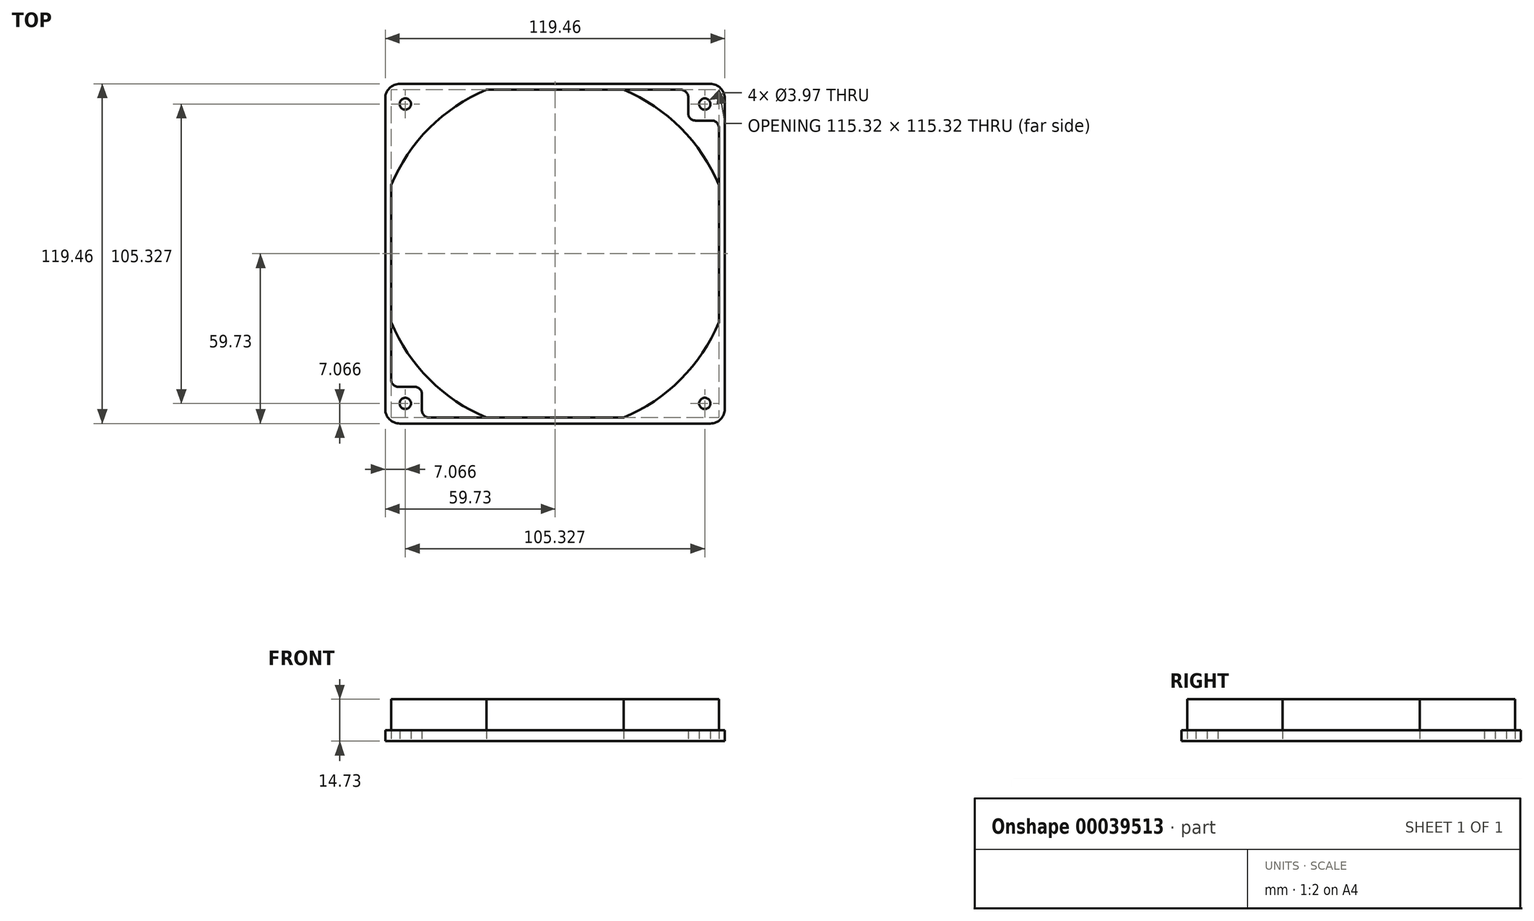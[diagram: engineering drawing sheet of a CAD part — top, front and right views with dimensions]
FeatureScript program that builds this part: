
annotation { "Feature Type Name" : "Feature", "Feature Type Description" : "" }
export const myFeature = defineFeature(function(context is Context, id is Id, definition is map)
    precondition{}
    {
        {
            var Q0;
            Q0=qCreatedBy(makeId("Top.planeOp"),FACE);
            var sketch = newSketch(context, id + "F0", { "sketchPlane" : qUnion([Q0])});
            skLineSegment(sketch, "E0", {"start": v(0, 0) * mm, "end": v(0, 233.62) * mm, "construction": true});
            skLineSegment(sketch, "E1.rect.bottom", {"start": v(-59.73, 59.73) * mm, "end": v(59.73, 59.73) * mm, "construction": true});
            skLineSegment(sketch, "E1.rect.top", {"start": v(-59.73, -59.73) * mm, "end": v(59.73, -59.73) * mm, "construction": true});
            skLineSegment(sketch, "E1.rect.left", {"start": v(-59.73, 59.73) * mm, "end": v(-59.73, -59.73) * mm, "construction": true});
            skLineSegment(sketch, "E1.rect.right", {"start": v(59.73, 59.73) * mm, "end": v(59.73, -59.73) * mm, "construction": true});
            skPoint(sketch, "E1.rect.middle", {"position": v(0, 0) * mm});
            skCircle(sketch, "E2", {"center": v(0, 0) * mm, "radius": 57.66 * mm, "construction": true});
            skLineSegment(sketch, "E3", {"start": v(-59.73, 0) * mm, "end": v(-59.73, 54.65) * mm});
            skLineSegment(sketch, "E4", {"start": v(0, 59.73) * mm, "end": v(-54.65, 59.73) * mm});
            skCircle(sketch, "E5", {"center": v(-52.66, 52.66) * mm, "radius": 1.98 * mm});
            skArc(sketch, "E6", {"start": v(-57.66, 0) * mm, "mid": v(-40.77, 40.77) * mm, "end": v(0, 57.66) * mm});
            skLineSegment(sketch, "E7", {"start": v(-57.66, 0) * mm, "end": v(-57.66, 44.3) * mm});
            skLineSegment(sketch, "E8", {"start": v(-55.12, 46.83) * mm, "end": v(-49.37, 46.83) * mm});
            skLineSegment(sketch, "E9", {"start": v(-46.83, 49.37) * mm, "end": v(-46.83, 55.12) * mm});
            skLineSegment(sketch, "E10", {"start": v(-44.3, 57.66) * mm, "end": v(0, 57.66) * mm});
            skArc(sketch, "E11", {"start": v(-57.66, 29.09) * mm, "mid": v(-45.66, 45.66) * mm, "end": v(-29.09, 57.66) * mm, "construction": true});
            skPoint(sketch, "E12.visualSharp", {"position": v(-57.66, 46.83) * mm});
            skArc(sketch, "E12.filletArc", {"start": v(-55.12, 46.83) * mm, "mid": v(-56.91, 46.09) * mm, "end": v(-57.66, 44.3) * mm});
            skPoint(sketch, "E13.visualSharp", {"position": v(-46.83, 46.83) * mm});
            skArc(sketch, "E13.filletArc", {"start": v(-49.37, 46.83) * mm, "mid": v(-47.58, 47.58) * mm, "end": v(-46.83, 49.37) * mm});
            skPoint(sketch, "E14.visualSharp", {"position": v(-46.83, 57.66) * mm});
            skArc(sketch, "E14.filletArc", {"start": v(-44.3, 57.66) * mm, "mid": v(-46.09, 56.91) * mm, "end": v(-46.83, 55.12) * mm});
            skPoint(sketch, "E15.visualSharp", {"position": v(-59.73, 59.73) * mm});
            skArc(sketch, "E15.filletArc", {"start": v(-54.65, 59.73) * mm, "mid": v(-58.24, 58.24) * mm, "end": v(-59.73, 54.65) * mm});
            skLineSegment(sketch, "E16", {"start": v(0, 0) * mm, "end": v(-142.77, 0) * mm, "construction": true});
            skArc(sketch, "E17.MirrorCS", {"start": v(49.37, 46.83) * mm, "mid": v(47.58, 47.58) * mm, "end": v(46.83, 49.37) * mm});
            skArc(sketch, "E18.MirrorCS", {"start": v(44.3, 57.66) * mm, "mid": v(46.09, 56.91) * mm, "end": v(46.83, 55.12) * mm});
            skLineSegment(sketch, "E19.MirrorCS", {"start": v(55.12, 46.83) * mm, "end": v(49.37, 46.83) * mm});
            skLineSegment(sketch, "E20.MirrorCS", {"start": v(46.83, 49.37) * mm, "end": v(46.83, 55.12) * mm});
            skCircle(sketch, "E21.MirrorC", {"center": v(52.66, 52.66) * mm, "radius": 1.98 * mm});
            skArc(sketch, "E22.MirrorCS", {"start": v(54.65, 59.73) * mm, "mid": v(58.24, 58.24) * mm, "end": v(59.73, 54.65) * mm});
            skArc(sketch, "E23.MirrorCS", {"start": v(55.12, 46.83) * mm, "mid": v(56.91, 46.09) * mm, "end": v(57.66, 44.3) * mm});
            skPoint(sketch, "E24.MirrorP", {"position": v(59.73, 59.73) * mm});
            skLineSegment(sketch, "E25.MirrorCS", {"start": v(57.66, 0) * mm, "end": v(57.66, 44.3) * mm});
            skArc(sketch, "E26.MirrorCS", {"start": v(57.66, 0) * mm, "mid": v(40.77, 40.77) * mm, "end": v(0, 57.66) * mm});
            skPoint(sketch, "E27.MirrorP", {"position": v(46.83, 57.66) * mm});
            skLineSegment(sketch, "E28.MirrorCS", {"start": v(59.73, 0) * mm, "end": v(59.73, 54.65) * mm});
            skLineSegment(sketch, "E29.MirrorCS", {"start": v(44.3, 57.66) * mm, "end": v(0, 57.66) * mm});
            skLineSegment(sketch, "E30.MirrorCS", {"start": v(0, 59.73) * mm, "end": v(54.65, 59.73) * mm});
            skArc(sketch, "E31.MirrorCS", {"start": v(57.66, 29.09) * mm, "mid": v(45.66, 45.66) * mm, "end": v(29.09, 57.66) * mm, "construction": true});
            skPoint(sketch, "E32.MirrorP", {"position": v(46.83, 46.83) * mm});
            skPoint(sketch, "E33.MirrorP", {"position": v(57.66, 46.83) * mm});
            skLineSegment(sketch, "E34.MirrorCS", {"start": v(-59.73, -59.73) * mm, "end": v(59.73, -59.73) * mm});
            skLineSegment(sketch, "E35.MirrorCS", {"start": v(55.12, -46.83) * mm, "end": v(49.37, -46.83) * mm});
            skArc(sketch, "E36.MirrorCS", {"start": v(54.65, -59.73) * mm, "mid": v(58.24, -58.24) * mm, "end": v(59.73, -54.65) * mm});
            skArc(sketch, "E37.MirrorCS", {"start": v(49.37, -46.83) * mm, "mid": v(47.58, -47.58) * mm, "end": v(46.83, -49.37) * mm});
            skArc(sketch, "E38.MirrorCS", {"start": v(-49.37, -46.83) * mm, "mid": v(-47.58, -47.58) * mm, "end": v(-46.83, -49.37) * mm});
            skArc(sketch, "E39.MirrorCS", {"start": v(-44.3, -57.66) * mm, "mid": v(-46.09, -56.91) * mm, "end": v(-46.83, -55.12) * mm});
            skLineSegment(sketch, "E40.MirrorCS", {"start": v(46.83, -49.37) * mm, "end": v(46.83, -55.12) * mm});
            skArc(sketch, "E41.MirrorCS", {"start": v(55.12, -46.83) * mm, "mid": v(56.91, -46.09) * mm, "end": v(57.66, -44.3) * mm});
            skArc(sketch, "E42.MirrorCS", {"start": v(-54.65, -59.73) * mm, "mid": v(-58.24, -58.24) * mm, "end": v(-59.73, -54.65) * mm});
            skArc(sketch, "E43.MirrorCS", {"start": v(44.3, -57.66) * mm, "mid": v(46.09, -56.91) * mm, "end": v(46.83, -55.12) * mm});
            skLineSegment(sketch, "E44.MirrorCS", {"start": v(-55.12, -46.83) * mm, "end": v(-49.37, -46.83) * mm});
            skLineSegment(sketch, "E45.MirrorCS", {"start": v(-46.83, -49.37) * mm, "end": v(-46.83, -55.12) * mm});
            skArc(sketch, "E46.MirrorCS", {"start": v(-55.12, -46.83) * mm, "mid": v(-56.91, -46.09) * mm, "end": v(-57.66, -44.3) * mm});
            skCircle(sketch, "E47.MirrorC", {"center": v(52.66, -52.66) * mm, "radius": 1.98 * mm});
            skCircle(sketch, "E48.MirrorC", {"center": v(-52.66, -52.66) * mm, "radius": 1.98 * mm});
            skArc(sketch, "E49.MirrorCS", {"start": v(57.66, 0) * mm, "mid": v(40.77, -40.77) * mm, "end": v(0, -57.66) * mm});
            skLineSegment(sketch, "E50.MirrorCS", {"start": v(57.66, 0) * mm, "end": v(57.66, -44.3) * mm});
            skArc(sketch, "E51.MirrorCS", {"start": v(-57.66, -29.09) * mm, "mid": v(-45.66, -45.66) * mm, "end": v(-29.09, -57.66) * mm, "construction": true});
            skArc(sketch, "E52.MirrorCS", {"start": v(57.66, -29.09) * mm, "mid": v(45.66, -45.66) * mm, "end": v(29.09, -57.66) * mm, "construction": true});
            skPoint(sketch, "E53.MirrorP", {"position": v(57.66, -46.83) * mm});
            skPoint(sketch, "E54.MirrorP", {"position": v(-57.66, -46.83) * mm});
            skPoint(sketch, "E55.MirrorP", {"position": v(59.73, -59.73) * mm});
            skLineSegment(sketch, "E56.MirrorCS", {"start": v(-59.73, 0) * mm, "end": v(-59.73, -54.65) * mm});
            skPoint(sketch, "E57.MirrorP", {"position": v(-59.73, -59.73) * mm});
            skLineSegment(sketch, "E58.MirrorCS", {"start": v(59.73, 0) * mm, "end": v(59.73, -54.65) * mm});
            skLineSegment(sketch, "E59.MirrorCS", {"start": v(-44.3, -57.66) * mm, "end": v(0, -57.66) * mm});
            skPoint(sketch, "E60.MirrorP", {"position": v(-46.83, -46.83) * mm});
            skLineSegment(sketch, "E61.MirrorCS", {"start": v(0, -59.73) * mm, "end": v(-54.65, -59.73) * mm});
            skLineSegment(sketch, "E62.MirrorCS", {"start": v(0, -59.73) * mm, "end": v(54.65, -59.73) * mm});
            skPoint(sketch, "E63.MirrorP", {"position": v(46.83, -57.66) * mm});
            skArc(sketch, "E64.MirrorCS", {"start": v(-57.66, 0) * mm, "mid": v(-40.77, -40.77) * mm, "end": v(0, -57.66) * mm});
            skLineSegment(sketch, "E65.MirrorCS", {"start": v(-57.66, 0) * mm, "end": v(-57.66, -44.3) * mm});
            skPoint(sketch, "E66.MirrorP", {"position": v(46.83, -46.83) * mm});
            skLineSegment(sketch, "E67.MirrorCS", {"start": v(44.3, -57.66) * mm, "end": v(0, -57.66) * mm});
            skPoint(sketch, "E68.MirrorP", {"position": v(-46.83, -57.66) * mm});
            skArc(sketch, "E69", {"start": v(-57.66, 24.14) * mm, "mid": v(-44.2, 44.2) * mm, "end": v(-24.14, 57.66) * mm});
            skLineSegment(sketch, "E70", {"start": v(-59.73, 0) * mm, "end": v(-57.66, 0) * mm, "construction": true});
            skLineSegment(sketch, "E71", {"start": v(-53.8, 35.71) * mm, "end": v(-52.08, 34.57) * mm, "construction": true});
            skCircle(sketch, "E72", {"center": v(0, 0) * mm, "radius": 64.58 * mm, "construction": true});
            skArc(sketch, "E73.MirrorCS", {"start": v(57.66, 24.14) * mm, "mid": v(44.2, 44.2) * mm, "end": v(24.14, 57.66) * mm});
            skArc(sketch, "E74.MirrorCS", {"start": v(-57.66, -24.14) * mm, "mid": v(-44.2, -44.2) * mm, "end": v(-24.14, -57.66) * mm});
            skArc(sketch, "E75.MirrorCS", {"start": v(57.66, -24.14) * mm, "mid": v(44.2, -44.2) * mm, "end": v(24.14, -57.66) * mm});
            skSolve(sketch);
        }
        {
            var Q0;
            Q0=makeQuery(id+"F0.imprint","IMPRINT",FACE,{"disambiguationData":[TD([[makeQuery(id+"F0.imprint","IMPRINT",EDGE,{"derivedFrom":sQuery(id+"F0.wireOp",EDGE,"E3")}),-1.0]])]});
            var Q1;
            Q1=makeQuery(id+"F0.imprint","IMPRINT",FACE,{"disambiguationData":[TD([[makeQuery(id+"F0.imprint","IMPRINT",EDGE,{"derivedFrom":sQuery(id+"F0.wireOp",EDGE,"E8")}),-1.0]])]});
            var Q2;
            Q2=makeQuery(id+"F0.imprint","IMPRINT",FACE,{"disambiguationData":[TD([[makeQuery(id+"F0.imprint","IMPRINT",EDGE,{"derivedFrom":sQuery(id+"F0.wireOp",EDGE,"E38.MirrorCS")}),1.0]])]});
            var Q3;
            Q3=makeQuery(id+"F0.imprint","IMPRINT",FACE,{"disambiguationData":[TD([[makeQuery(id+"F0.imprint","IMPRINT",EDGE,{"derivedFrom":sQuery(id+"F0.wireOp",EDGE,"E35.MirrorCS")}),-1.0]])]});
            var Q4;
            Q4=makeQuery(id+"F0.imprint","IMPRINT",FACE,{"disambiguationData":[TD([[makeQuery(id+"F0.imprint","IMPRINT",EDGE,{"derivedFrom":sQuery(id+"F0.wireOp",EDGE,"E17.MirrorCS")}),1.0]])]});
            extrude(context, id + "F1", {"entities" : qUnion([Q0, Q1, Q2, Q3, Q4]), "depth" : 3.8 * mm});
        }
        {
            var Q0;
            Q0=makeQuery(id+"F1.opExtrude","CAP_FACE",FACE,{"disambiguationData":[OSD([sQuery(id+"F0.wireOp",EDGE,"E3"),sQuery(id+"F0.wireOp",EDGE,"E4"),sQuery(id+"F0.wireOp",EDGE,"E5"),sQuery(id+"F0.wireOp",EDGE,"E7"),sQuery(id+"F0.wireOp",EDGE,"E10"),sQuery(id+"F0.wireOp",EDGE,"E15.filletArc"),sQuery(id+"F0.wireOp",EDGE,"E21.MirrorC"),sQuery(id+"F0.wireOp",EDGE,"E22.MirrorCS"),sQuery(id+"F0.wireOp",EDGE,"E25.MirrorCS"),sQuery(id+"F0.wireOp",EDGE,"E28.MirrorCS"),sQuery(id+"F0.wireOp",EDGE,"E29.MirrorCS"),sQuery(id+"F0.wireOp",EDGE,"E30.MirrorCS"),sQuery(id+"F0.wireOp",EDGE,"E36.MirrorCS"),sQuery(id+"F0.wireOp",EDGE,"E42.MirrorCS"),sQuery(id+"F0.wireOp",EDGE,"E47.MirrorC"),sQuery(id+"F0.wireOp",EDGE,"E48.MirrorC"),sQuery(id+"F0.wireOp",EDGE,"E50.MirrorCS"),sQuery(id+"F0.wireOp",EDGE,"E56.MirrorCS"),sQuery(id+"F0.wireOp",EDGE,"E58.MirrorCS"),sQuery(id+"F0.wireOp",EDGE,"E59.MirrorCS"),sQuery(id+"F0.wireOp",EDGE,"E61.MirrorCS"),sQuery(id+"F0.wireOp",EDGE,"E62.MirrorCS"),sQuery(id+"F0.wireOp",EDGE,"E65.MirrorCS"),sQuery(id+"F0.wireOp",EDGE,"E67.MirrorCS"),sQuery(id+"F0.wireOp",EDGE,"E69"),sQuery(id+"F0.wireOp",EDGE,"E73.MirrorCS"),sQuery(id+"F0.wireOp",EDGE,"E74.MirrorCS"),sQuery(id+"F0.wireOp",EDGE,"E75.MirrorCS")])],"isStart":false});
            var sketch = newSketch(context, id + "F2", { "sketchPlane" : qUnion([Q0])});
            skArc(sketch, "E76", {"start": v(-57.66, 24.14) * mm, "mid": v(-44.2, 44.2) * mm, "end": v(-24.14, 57.66) * mm});
            skArc(sketch, "E77", {"start": v(-59.73, 28.18) * mm, "mid": v(-46.7, 46.7) * mm, "end": v(-28.18, 59.73) * mm});
            skLineSegment(sketch, "E78", {"start": v(-59.73, 0) * mm, "end": v(-59.73, 28.18) * mm});
            skLineSegment(sketch, "E79", {"start": v(-28.18, 59.73) * mm, "end": v(0, 59.73) * mm});
            skLineSegment(sketch, "E80", {"start": v(-57.66, 0) * mm, "end": v(-57.66, 24.14) * mm});
            skLineSegment(sketch, "E81", {"start": v(-24.14, 57.66) * mm, "end": v(0, 57.66) * mm});
            skLineSegment(sketch, "E82.MirrorCS", {"start": v(24.14, 57.66) * mm, "end": v(0, 57.66) * mm});
            skLineSegment(sketch, "E83.MirrorCS", {"start": v(57.66, 0) * mm, "end": v(57.66, 24.14) * mm});
            skArc(sketch, "E84.MirrorCS", {"start": v(57.66, 24.14) * mm, "mid": v(44.2, 44.2) * mm, "end": v(24.14, 57.66) * mm});
            skArc(sketch, "E85.MirrorCS", {"start": v(59.73, 28.18) * mm, "mid": v(46.7, 46.7) * mm, "end": v(28.18, 59.73) * mm});
            skLineSegment(sketch, "E86.MirrorCS", {"start": v(59.73, 0) * mm, "end": v(59.73, 28.18) * mm});
            skLineSegment(sketch, "E87.MirrorCS", {"start": v(28.18, 59.73) * mm, "end": v(0, 59.73) * mm});
            skLineSegment(sketch, "E88.MirrorCS", {"start": v(24.14, -57.66) * mm, "end": v(0, -57.66) * mm});
            skLineSegment(sketch, "E89.MirrorCS", {"start": v(-24.14, -57.66) * mm, "end": v(0, -57.66) * mm});
            skLineSegment(sketch, "E90.MirrorCS", {"start": v(-57.66, 0) * mm, "end": v(-57.66, -24.14) * mm});
            skLineSegment(sketch, "E91.MirrorCS", {"start": v(-28.18, -59.73) * mm, "end": v(0, -59.73) * mm});
            skLineSegment(sketch, "E92.MirrorCS", {"start": v(-59.73, 0) * mm, "end": v(-59.73, -28.18) * mm});
            skArc(sketch, "E93.MirrorCS", {"start": v(-59.73, -28.18) * mm, "mid": v(-46.7, -46.7) * mm, "end": v(-28.18, -59.73) * mm});
            skArc(sketch, "E94.MirrorCS", {"start": v(-57.66, -24.14) * mm, "mid": v(-44.2, -44.2) * mm, "end": v(-24.14, -57.66) * mm});
            skLineSegment(sketch, "E95.MirrorCS", {"start": v(57.66, 0) * mm, "end": v(57.66, -24.14) * mm});
            skArc(sketch, "E96.MirrorCS", {"start": v(57.66, -24.14) * mm, "mid": v(44.2, -44.2) * mm, "end": v(24.14, -57.66) * mm});
            skLineSegment(sketch, "E97.MirrorCS", {"start": v(28.18, -59.73) * mm, "end": v(0, -59.73) * mm});
            skLineSegment(sketch, "E98.MirrorCS", {"start": v(59.73, 0) * mm, "end": v(59.73, -28.18) * mm});
            skArc(sketch, "E99.MirrorCS", {"start": v(59.73, -28.18) * mm, "mid": v(46.7, -46.7) * mm, "end": v(28.18, -59.73) * mm});
            skCircle(sketch, "E100", {"center": v(0, 0) * mm, "radius": 77.98 * mm});
            skCircle(sketch, "E101", {"center": v(0, 0) * mm, "radius": 69.4 * mm});
            skSolve(sketch);
        }
        {
            var Q0;
            Q0=makeQuery(id+"F2.imprint","IMPRINT",FACE,{"disambiguationData":[TD([[makeQuery(id+"F2.imprint","IMPRINT",EDGE,{"derivedFrom":sQuery(id+"F2.wireOp",EDGE,"E76")}),1.0]])]});
            extrude(context, id + "F3", {"entities" : qUnion([Q0]), "operationType" : NewBodyOperationType.ADD, "depth" : (3.25 - 1.1) * 5.08 * mm});
        }
    });
